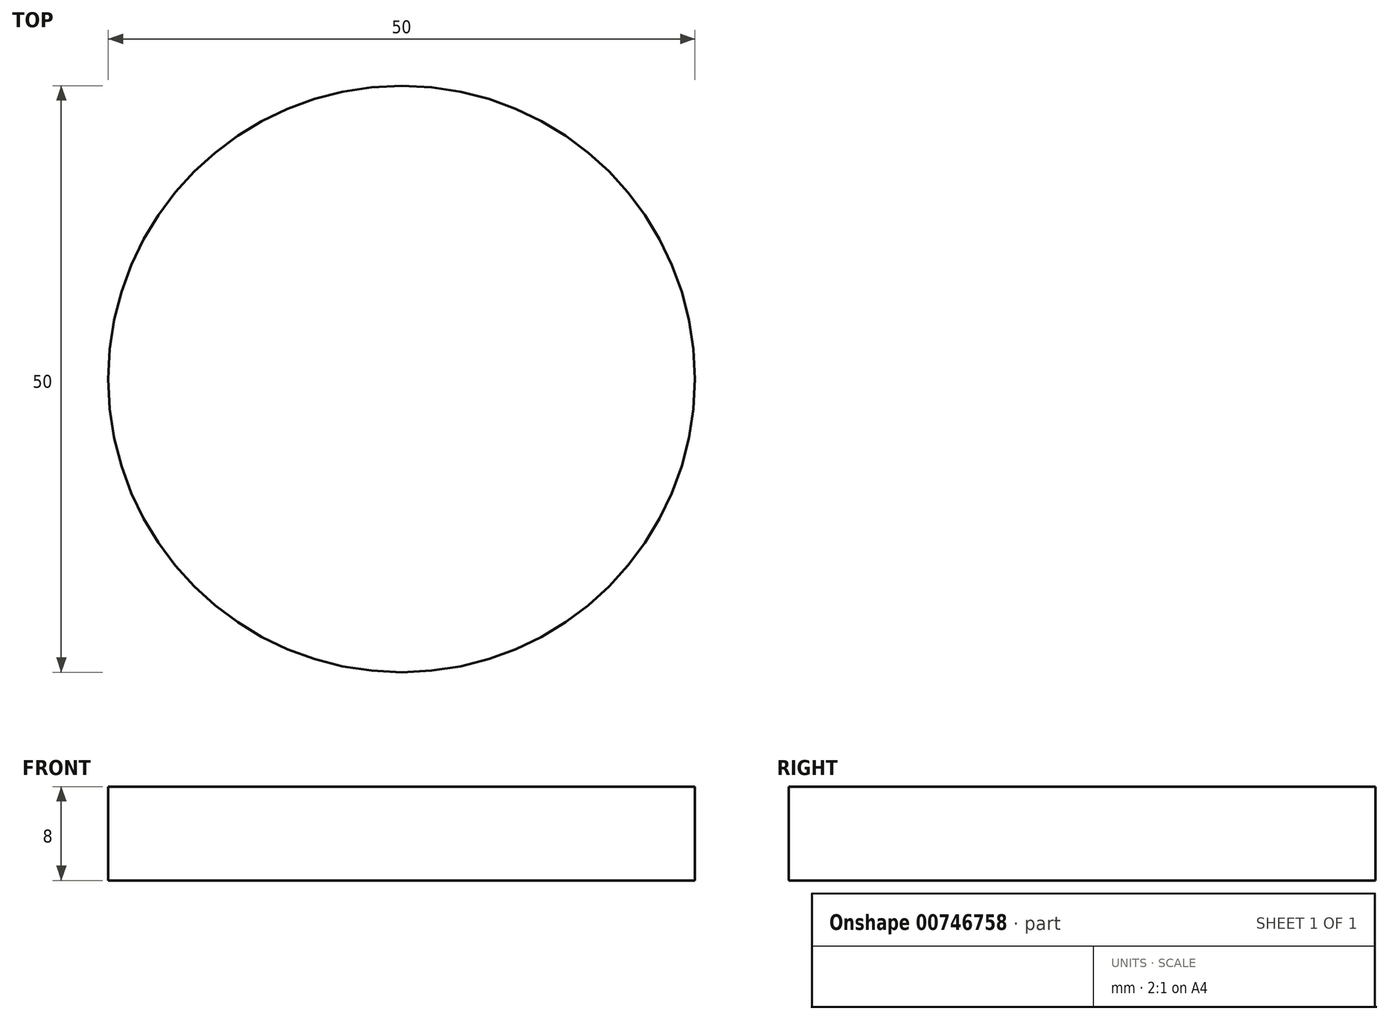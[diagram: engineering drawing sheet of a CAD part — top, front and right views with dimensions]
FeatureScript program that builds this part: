
annotation { "Feature Type Name" : "Feature", "Feature Type Description" : "" }
export const myFeature = defineFeature(function(context is Context, id is Id, definition is map)
    precondition{}
    {
        {
            var Q0;
            Q0=qCreatedBy(makeId("Top.planeOp"),FACE);
            var sketch = newSketch(context, id + "F0", { "sketchPlane" : qUnion([Q0])});
            skCircle(sketch, "E0", {"center": v(0, 0) * mm, "radius": 25 * mm});
            skSolve(sketch);
        }
        {
            var Q0;
            Q0=makeQuery(id+"F0.imprint","IMPRINT",FACE,{"disambiguationData":[TD([[makeQuery(id+"F0.imprint","IMPRINT",EDGE,{"derivedFrom":sQuery(id+"F0.wireOp",EDGE,"E0")}),1.0]])]});
            extrude(context, id + "F1", {"entities" : qUnion([Q0]), "depth" : 8 * mm, "offsetDistance" : 25 * mm});
        }
    });
